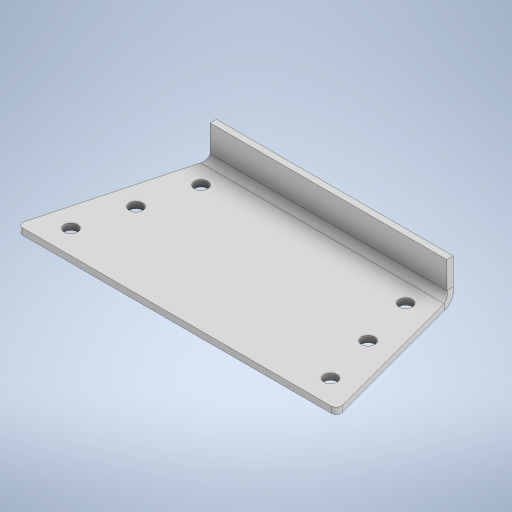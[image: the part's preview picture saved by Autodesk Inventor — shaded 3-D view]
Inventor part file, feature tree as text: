
AUTODESK INVENTOR PART (.ipt)
format: ipt  version: 2024.2 (Build 282272000, 272)  size: 284,672 bytes
history: native  units: mm
features: sheet_metal_op x4, sketch x3, other x2, hole x1, chamfer x1, mirror x1, projected_geometry x1
ambient origin geometry x8: Origin, YZ Plane, XZ Plane, XY Plane, X Axis, Y Axis, Z Axis, Center Point
bodies: Solid1 (feature_tree)
feature tree (13):
  sheet_metal_op  "Face1"
  hole  "Hole1"  [1 undecoded]
  chamfer  "Corner Round1"
  mirror  "Mirror1"
  sheet_metal_op  "Flange1"
  sketch  "Sketch1"  dims[d0=300.0mm d1=200.0mm]
  other  "Plate1"
  sketch  "Sketch3"  dims[d2=15.0deg]
  projected_geometry  "Projected Loop1"
  sketch  "Sketch4"  dims[d3=8.0mm d4=17.0mm d5=6.0mm d6=4.0mm d7=2.0mm d8=90.0deg d9=8.0mm d10=20.594885mm d11=30.0mm d12=40.0mm d13=30.0mm d14=6.0mm d15=8.0mm d16=4.0mm d17=16.0mm d18=8.0mm d19=50.0mm d20=90.0deg d21=8.0mm d22=32.0mm d23=8.0mm d24=8.0mm]
  other  "Plate2"
  sheet_metal_op  "Bend1"
  sheet_metal_op  "Corner1"
note: 1 required parameter value undecoded (feature->parameter linkage not recoverable at this tier; creation-order binding heuristic only, values carry confidence <= 0.55)
